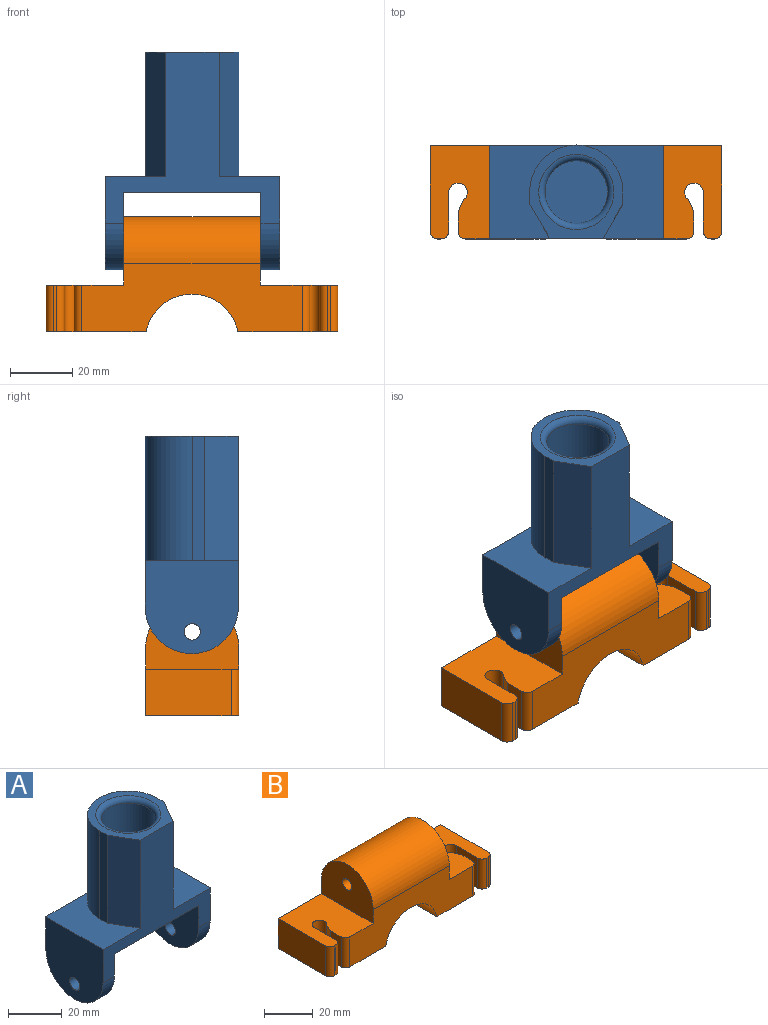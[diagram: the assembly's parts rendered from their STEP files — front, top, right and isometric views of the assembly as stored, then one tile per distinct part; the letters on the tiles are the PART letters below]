
ASSEMBLY  parts=2 mates=1
PART A: 22 faces, bbox 56.2x30x70 mm
  f0: plane 44.2x30mm, normal (0,0,-1), area 1326mm2, adj f2,f10,f14,f15
  f1: plane 40x3.91mm, normal (-1,-0.01,0), area 156.5mm2, adj f5,f6,f12,f20
  f2: plane 56.2x55mm, normal (0,-1,0), area 1091.3mm2, adj f0,f6,f8,f9,f11,f12,f14,f15
  f3: plane 40x3.85mm, normal (1,0,0), area 153.9mm2, adj f5,f6,f11,f21
  f4: cylinder r=10.1mm len=38mm, axis (0,0,-1), area 2411.5mm2, adj f7,f13
  f5: cylinder r=15mm len=40mm, axis (0,0,-1), area 1897.1mm2, adj f1,f3,f6,f11,f12
  f6: plane 30x30mm, normal (0,0,1), area 273.3mm2, adj f1,f2,f3,f5,f7,f20,f21
  f7: torus R=12.1mm, axis (0,0,1), area 213.7mm2, adj f4,f6
  f8: plane 30x30mm, normal (1,0,0), area 781.4mm2, adj f2,f10,f11,f17,f19
  f9: plane 30x30mm, normal (-1,0,0), area 781.4mm2, adj f2,f10,f12,f16,f18
  f10: plane 56.2x15mm, normal (0,1,0), area 401mm2, adj f0,f8,f9,f11,f12,f14,f15,f16
  f11: plane 30x28.1mm, normal (0,0,1), area 476.2mm2, adj f2,f3,f5,f8,f10,f21
  f12: plane 30x28.1mm, normal (0,0,1), area 476.5mm2, adj f1,f2,f5,f9,f10,f20
  f13: plane 20.2x20.2mm, normal (0,0,1), area 320.5mm2, adj f4
  f14: plane 30x25mm, normal (-1,0,0), area 631.4mm2, adj f0,f2,f10,f17,f19
  f15: plane 30x25mm, normal (1,0,0), area 631.4mm2, adj f0,f2,f10,f16,f18
  f16: cylinder r=15mm len=30mm, axis (1,0,0), area 282.7mm2, adj f2,f9,f10,f15
  f17: cylinder r=15mm len=30mm, axis (1,0,0), area 282.7mm2, adj f2,f8,f10,f14
  f18: cylinder r=2.65mm len=6mm, axis (1,0,0), area 99.9mm2, adj f9,f15
  f19: cylinder r=2.65mm len=6mm, axis (1,0,0), area 99.9mm2, adj f8,f14
  f20: plane 40x10.94mm, normal (-0.86,-0.5,0), area 505.8mm2, adj f1,f2,f6,f12
  f21: plane 40x11mm, normal (0.87,-0.5,0), area 508.1mm2, adj f2,f3,f6,f11
PART B: 41 faces, bbox 94x30x37 mm
  f0: plane 30x25mm, normal (0,0,1), area 677mm2, adj f2,f4,f6,f8,f9,f28,f29,f31
  f1: plane 30x25mm, normal (0,0,1), area 677mm2, adj f3,f4,f5,f7,f8,f27,f30,f33
  f2: plane 15x6.26mm, normal (-1,0,0), area 93.8mm2, adj f0,f14,f31,f39
  f3: plane 15x6.26mm, normal (1,0,0), area 93.8mm2, adj f1,f13,f33,f40
  f4: plane 71x22mm, normal (0,-1,0), area 1104.8mm2, adj f0,f1,f6,f7,f11,f12,f13,f14
  f5: plane 15x1mm, normal (0,-1,0), area 15mm2, adj f1,f13,f34,f36
  f6: plane 30x22mm, normal (-1,0,0), area 541.4mm2, adj f0,f4,f8,f10,f11
  f7: plane 30x22mm, normal (1,0,0), area 541.4mm2, adj f1,f4,f8,f10,f11
  f8: plane 94x22mm, normal (0,1,0), area 1449.8mm2, adj f0,f1,f6,f7,f11,f12,f13,f14
  f9: plane 15x1mm, normal (0,-1,0), area 15mm2, adj f0,f14,f32,f35
  f10: cylinder r=2.65mm len=44mm, axis (1,0,0), area 732.6mm2, adj f6,f7
  f11: cylinder r=15mm len=44mm, axis (-1,0,0), area 2073.5mm2, adj f4,f6,f7,f8
  f12: cylinder r=15.1mm len=30mm, axis (0,-1,0), area 1241.9mm2, adj f4,f8,f13,f14
  f13: plane 32.2x30mm, normal (0,0,-1), area 874.5mm2, adj f3,f4,f5,f8,f12,f21,f23,f25
  f14: plane 32.2x30mm, normal (0,0,-1), area 874.5mm2, adj f2,f4,f8,f9,f12,f15,f17,f19
  f15: cylinder r=1.4mm len=17mm, axis (0,0,-1), area 149.5mm2, adj f14,f16
  f16: cone r=0mm half-angle=59deg, axis (0,0,-1), area 7.2mm2, adj f15
  f17: cylinder r=1.4mm len=17mm, axis (0,0,-1), area 149.5mm2, adj f14,f18
  f18: cone r=0mm half-angle=59deg, axis (0,0,-1), area 7.2mm2, adj f17
  f19: cylinder r=1.4mm len=17mm, axis (0,0,-1), area 149.5mm2, adj f14,f20
  f20: cone r=0mm half-angle=59deg, axis (0,0,-1), area 7.2mm2, adj f19
  f21: cylinder r=1.4mm len=17mm, axis (0,0,-1), area 149.5mm2, adj f13,f22
  f22: cone r=0mm half-angle=59deg, axis (0,0,-1), area 7.2mm2, adj f21
  f23: cylinder r=1.4mm len=17mm, axis (0,0,-1), area 149.5mm2, adj f13,f24
  f24: cone r=0mm half-angle=59deg, axis (0,0,-1), area 7.2mm2, adj f23
  f25: cylinder r=1.4mm len=17mm, axis (0,0,-1), area 149.5mm2, adj f13,f26
  f26: cone r=0mm half-angle=59deg, axis (0,0,-1), area 7.2mm2, adj f25
  f27: plane 27.5x15mm, normal (1,0,0), area 412.5mm2, adj f1,f8,f13,f36
  f28: plane 27.5x15mm, normal (-1,0,0), area 412.5mm2, adj f0,f8,f14,f35
  f29: plane 15x12.5mm, normal (1,0,0), area 187.5mm2, adj f0,f14,f32,f38
  f30: plane 15x12.5mm, normal (-1,0,0), area 187.5mm2, adj f1,f13,f34,f37
  f31: cylinder r=2.5mm len=15mm, axis (0,0,-1), area 58.9mm2, adj f0,f2,f4,f14
  f32: cylinder r=2.5mm len=15mm, axis (0,0,1), area 58.9mm2, adj f0,f9,f14,f29
  f33: cylinder r=2.5mm len=15mm, axis (0,0,1), area 58.9mm2, adj f1,f3,f4,f13
  f34: cylinder r=2.5mm len=15mm, axis (0,0,-1), area 58.9mm2, adj f1,f5,f13,f30
  f35: cylinder r=2.5mm len=15mm, axis (0,0,-1), area 58.9mm2, adj f0,f9,f14,f28
  f36: cylinder r=2.5mm len=15mm, axis (0,0,-1), area 58.9mm2, adj f1,f5,f13,f27
  f37: cylinder r=3mm len=15mm, axis (0,0,1), area 181.7mm2, adj f1,f13,f30,f40
  f38: cylinder r=3mm len=15mm, axis (0,0,1), area 181.7mm2, adj f0,f14,f29,f39
  f39: plane 15x3.9mm, normal (-0.9,0.43,0), area 65mm2, adj f0,f2,f14,f38
  f40: plane 15x3.9mm, normal (0.9,0.43,0), area 65mm2, adj f1,f3,f13,f37
PLACE A t=(37.85,-8.24,9.02)mm
PLACE B t=(-23.72,18.81,-43.98)mm
MATE pin_slot A.f18 <-> B.f10  axis (1,0,0) through (15.75,-8.24,-13.98)mm
